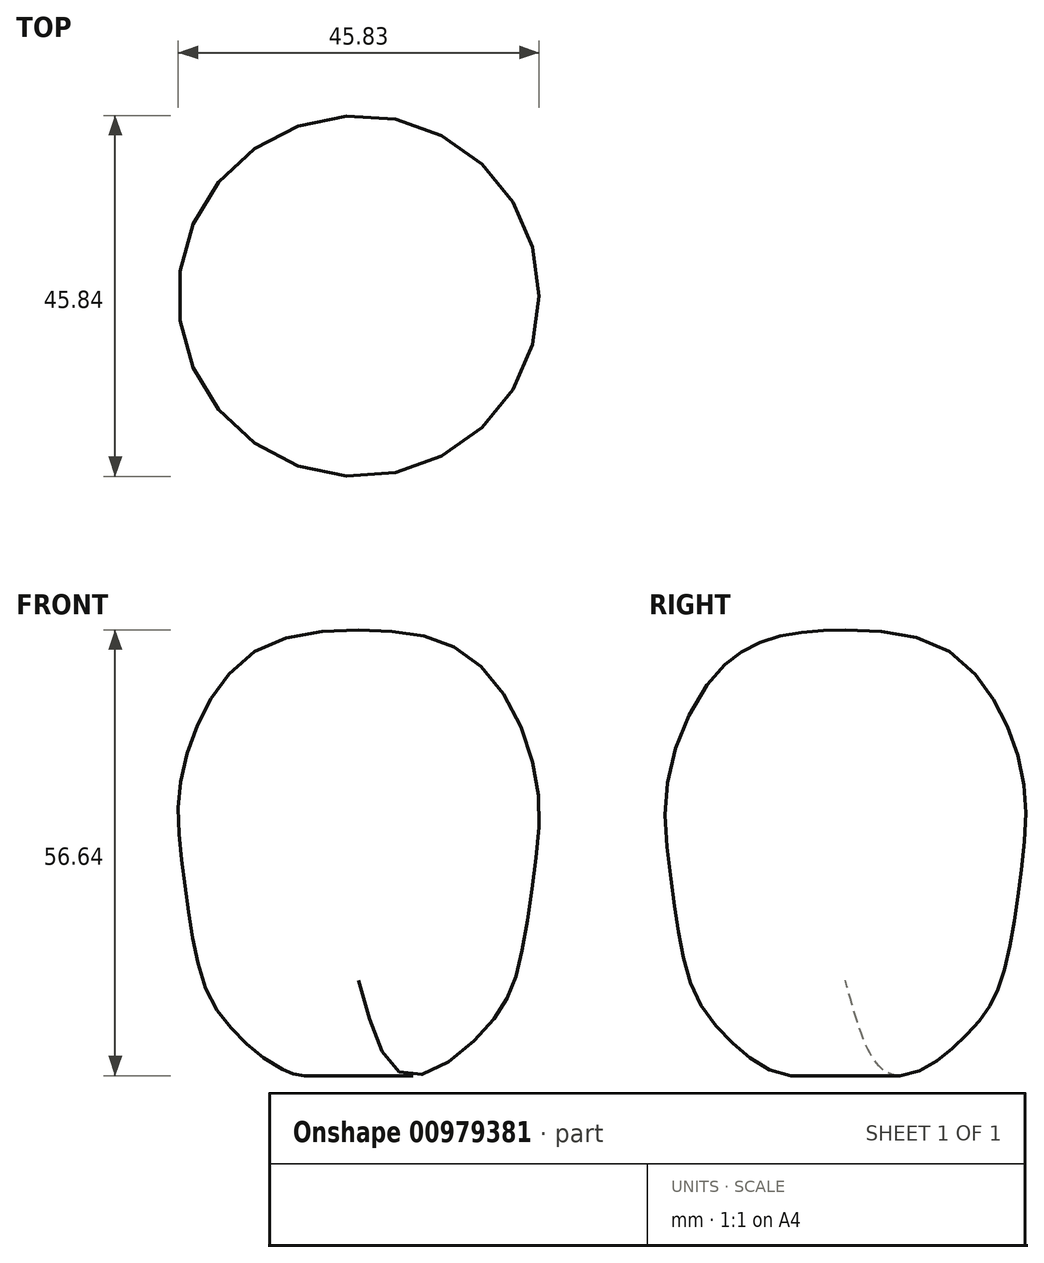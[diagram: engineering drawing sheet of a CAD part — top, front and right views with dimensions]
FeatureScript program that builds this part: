
annotation { "Feature Type Name" : "Feature", "Feature Type Description" : "" }
export const myFeature = defineFeature(function(context is Context, id is Id, definition is map)
    precondition{}
    {
        {
            var Q0;
            Q0=qCreatedBy(makeId("Front.planeOp"),FACE);
            var sketch = newSketch(context, id + "F0", { "sketchPlane" : qUnion([Q0])});
            skLineSegment(sketch, "E0.left", {"start": v(0, 63.83) * mm, "end": v(0, 19.31) * mm});
            skFitSpline(sketch, "E1", {"points": [v(0, 63.83) * mm, v(13.73, 60.7) * mm, v(22.35, 45.97) * mm, v(22.2, 32.33) * mm, v(20.07, 20.17) * mm, v(16.02, 13.02) * mm, v(6.14, 7.27) * mm, v(0, 19.31) * mm], "startDerivative": vector(98, -3.46) * mm, "endDerivative": vector(-30.38, 115.59) * mm});
            skSolve(sketch);
        }
        {
            var Q0;
            Q0 = qSketchRegion(id + "F0", true);
            var Q1;
            Q1=sQuery(id+"F0.wireOp",EDGE,"E0.left");
            revolve(context, id + "F1", {"surfaceOperationType" : NewSurfaceOperationType.NEW, "entities" : qUnion([Q0]), "axis" : qUnion([Q1]), "revolveType" : RevolveType.FULL});
        }
    });
